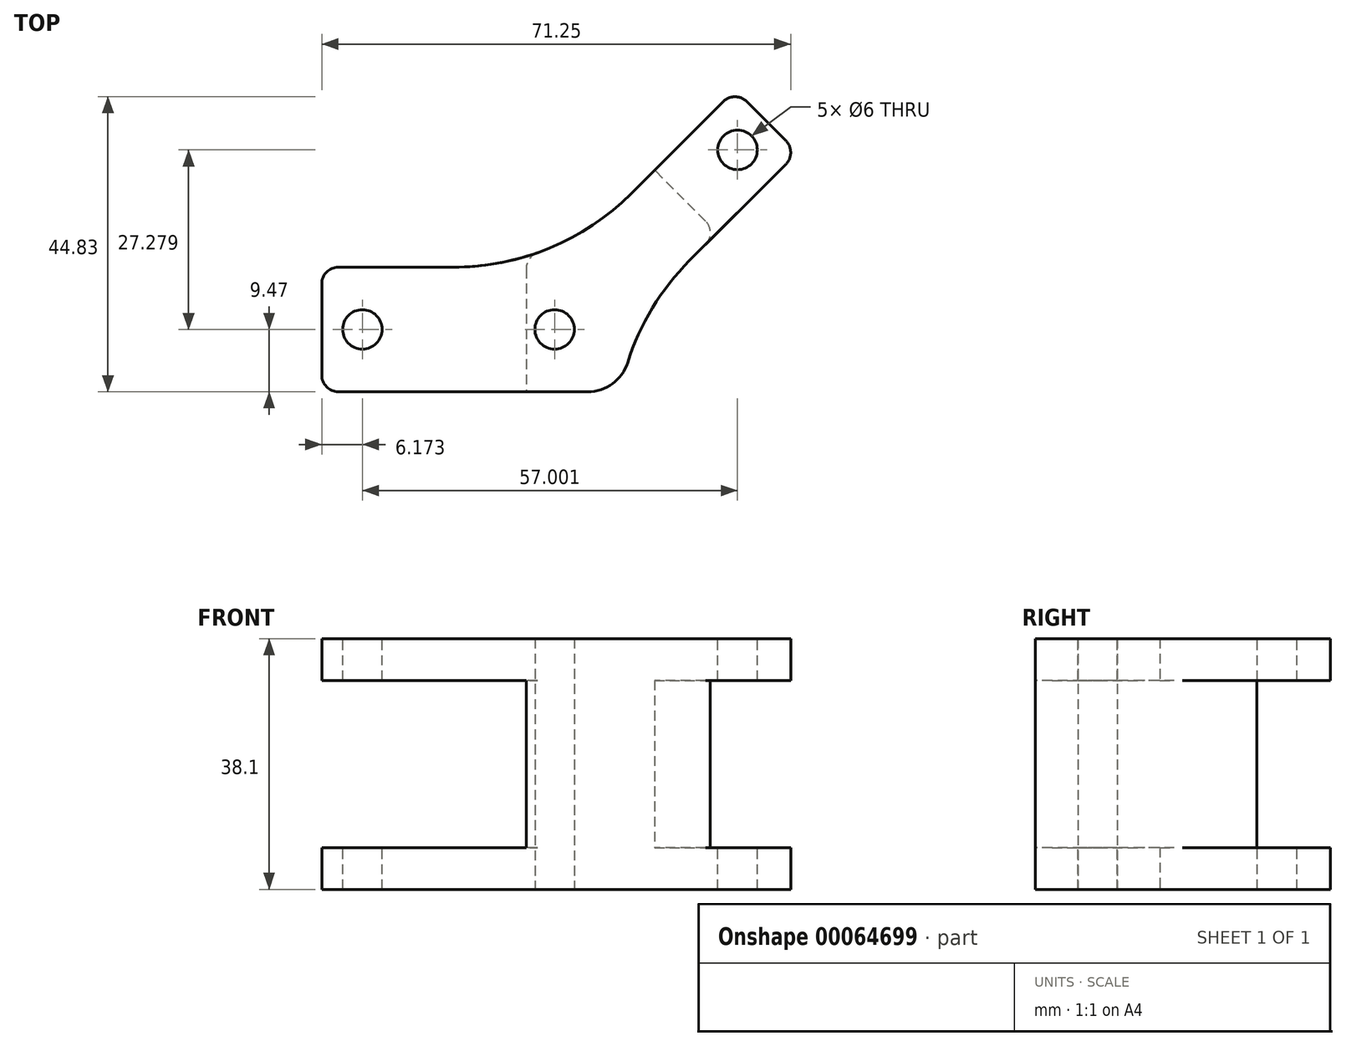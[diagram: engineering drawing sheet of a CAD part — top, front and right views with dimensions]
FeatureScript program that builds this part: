
annotation { "Feature Type Name" : "Feature", "Feature Type Description" : "" }
export const myFeature = defineFeature(function(context is Context, id is Id, definition is map)
    precondition{}
    {
        {
            var Q0;
            Q0=qCreatedBy(makeId("Top.planeOp"),FACE);
            var sketch = newSketch(context, id + "F0", { "sketchPlane" : qUnion([Q0])});
            skCircle(sketch, "E0", {"center": v(0, 0) * mm, "radius": 6 * mm});
            skLineSegment(sketch, "E1.rect.bottom", {"start": v(19.96, -18.93) * mm, "end": v(-19.96, -18.93) * mm});
            skLineSegment(sketch, "E1.rect.top", {"start": v(19.96, 18.93) * mm, "end": v(-19.96, 18.93) * mm});
            skLineSegment(sketch, "E1.rect.left", {"start": v(19.96, -18.93) * mm, "end": v(19.96, 18.93) * mm});
            skLineSegment(sketch, "E1.rect.right", {"start": v(-19.96, -18.93) * mm, "end": v(-19.96, 18.93) * mm});
            skSolve(sketch);
        }
        {
            var Q0;
            Q0=makeQuery(id+"F0.imprint","IMPRINT",FACE,{"disambiguationData":[TD([[makeQuery(id+"F0.imprint","IMPRINT",EDGE,{"derivedFrom":sQuery(id+"F0.wireOp",EDGE,"E0")}),-1.0]])]});
            extrude(context, id + "F1", {"entities" : qUnion([Q0]), "depth" : 76.2 * mm});
        }
        {
            var Q0;
            Q0=makeQuery(id+"F1.opExtrude","SWEPT_FACE",FACE,{"disambiguationData":[OSD([sQuery(id+"F0.wireOp",EDGE,"E1.rect.right")])]});
            extrude(context, id + "F2", {"entities" : qUnion([Q0]), "operationType" : NewBodyOperationType.ADD, "depth" : 38.1 * mm});
        }
        {
            var Q0;
            Q0=makeQuery(id+"F1.opExtrude","SWEPT_EDGE",EDGE,{"disambiguationData":[OSD([sQuery(id+"F0.wireOp",EDGE,"E1.rect.top"),sQuery(id+"F0.wireOp",EDGE,"E1.rect.left")])]});
            chamfer(context, id + "F3", {"entities" : qUnion([Q0]), "width" : 19.05 * mm, "tangentPropagation" : true});
        }
        {
            var Q0;
            Q0=makeQuery(id+"F3.opChamfer","BLEND_FACE",FACE,{"disambiguationData":[OSD([sQuery(id+"F0.wireOp",EDGE,"E1.rect.top"),sQuery(id+"F0.wireOp",EDGE,"E1.rect.left")])]});
            extrude(context, id + "F4", {"entities" : qUnion([Q0]), "operationType" : NewBodyOperationType.ADD, "depth" : 76.2 * mm});
        }
        {
            var Q0;
            {var subQ0=sQuery(id+"F0.wireOp",EDGE,"E1.rect.left");var subQ1=sQuery(id+"F0.wireOp",EDGE,"E1.rect.top");Q0=makeQuery(id+"F4.boolean.opBoolean","MERGE",EDGE,{"derivedFrom":[makeQuery(id+"F3.opChamfer","BLEND_EDGE",EDGE,{"blendedFrom":[makeQuery(id+"F1.opExtrude","SWEPT_EDGE",EDGE,{"disambiguationData":[OSD([subQ1,subQ0])]}),makeQuery(id+"F1.opExtrude","SWEPT_FACE",FACE,{"disambiguationData":[OSD([subQ0])]})],"blendedInto":[makeQuery(id+"F1.opExtrude","SWEPT_FACE",FACE,{"disambiguationData":[OSD([subQ0])]})]}),makeQuery(id+"F4.opExtrude","CAP_EDGE",EDGE,{"disambiguationData":[OSD([subQ1,subQ0])],"isStart":true})]});}
            fillet(context, id + "F5", {"entities" : qUnion([Q0]), "radius" : 76.2 * mm, "tangentPropagation" : true, "allowEdgeOverflow" : false});
        }
        {
            var Q0;
            {var subQ0=sQuery(id+"F0.wireOp",EDGE,"E1.rect.bottom");var subQ1=sQuery(id+"F0.wireOp",EDGE,"E1.rect.left");var subQ2=sQuery(id+"F0.wireOp",EDGE,"E1.rect.top");Q0=makeQuery(id+"F5.opFillet","BLEND_EDGE",EDGE,{"blendedFrom":[makeQuery(id+"F4.boolean.opBoolean","MERGE",EDGE,{"derivedFrom":[makeQuery(id+"F3.opChamfer","BLEND_EDGE",EDGE,{"blendedFrom":[makeQuery(id+"F1.opExtrude","SWEPT_EDGE",EDGE,{"disambiguationData":[OSD([subQ2,subQ1])]}),makeQuery(id+"F1.opExtrude","SWEPT_FACE",FACE,{"disambiguationData":[OSD([subQ1])]})],"blendedInto":[makeQuery(id+"F1.opExtrude","SWEPT_FACE",FACE,{"disambiguationData":[OSD([subQ1])]})]}),makeQuery(id+"F4.opExtrude","CAP_EDGE",EDGE,{"disambiguationData":[OSD([subQ2,subQ1])],"isStart":true})]}),makeQuery(id+"F2.boolean.opBoolean","MERGE",FACE,{"derivedFrom":[makeQuery(id+"F1.opExtrude","SWEPT_FACE",FACE,{"disambiguationData":[OSD([subQ0])]}),makeQuery(id+"F2.opExtrude","SWEPT_FACE",FACE,{"disambiguationData":[OSD([subQ0,sQuery(id+"F0.wireOp",EDGE,"E1.rect.right")])]})]})],"blendedInto":[makeQuery(id+"F2.boolean.opBoolean","MERGE",FACE,{"derivedFrom":[makeQuery(id+"F1.opExtrude","SWEPT_FACE",FACE,{"disambiguationData":[OSD([subQ0])]}),makeQuery(id+"F2.opExtrude","SWEPT_FACE",FACE,{"disambiguationData":[OSD([subQ0,sQuery(id+"F0.wireOp",EDGE,"E1.rect.right")])]})]})]});}
            fillet(context, id + "F6", {"entities" : qUnion([Q0]), "radius" : 12.7 * mm, "tangentPropagation" : true, "allowEdgeOverflow" : false});
        }
        {
            var Q0;
            {var subQ0=sQuery(id+"F0.wireOp",EDGE,"E1.rect.right");var subQ1=sQuery(id+"F0.wireOp",EDGE,"E1.rect.left");var subQ2=sQuery(id+"F0.wireOp",EDGE,"E1.rect.top");Q0=makeQuery(id+"F4.boolean.opBoolean","MERGE",EDGE,{"derivedFrom":[makeQuery(id+"F3.opChamfer","BLEND_EDGE",EDGE,{"blendedFrom":[makeQuery(id+"F1.opExtrude","SWEPT_EDGE",EDGE,{"disambiguationData":[OSD([subQ2,subQ1])]}),makeQuery(id+"F2.boolean.opBoolean","MERGE",FACE,{"derivedFrom":[makeQuery(id+"F1.opExtrude","SWEPT_FACE",FACE,{"disambiguationData":[OSD([subQ2])]}),makeQuery(id+"F2.opExtrude","SWEPT_FACE",FACE,{"disambiguationData":[OSD([subQ2,subQ0])]})]})],"blendedInto":[makeQuery(id+"F2.boolean.opBoolean","MERGE",FACE,{"derivedFrom":[makeQuery(id+"F1.opExtrude","SWEPT_FACE",FACE,{"disambiguationData":[OSD([subQ2])]}),makeQuery(id+"F2.opExtrude","SWEPT_FACE",FACE,{"disambiguationData":[OSD([subQ2,subQ0])]})]})]}),makeQuery(id+"F4.opExtrude","CAP_EDGE",EDGE,{"disambiguationData":[OSD([subQ2,subQ1,subQ0])],"isStart":true})]});}
            fillet(context, id + "F7", {"entities" : qUnion([Q0]), "radius" : 76.2 * mm, "tangentPropagation" : true, "allowEdgeOverflow" : false});
        }
        {
            var Q0;
            Q0=makeQuery(id+"F4.opExtrude","SWEPT_FACE",FACE,{"disambiguationData":[OSD([sQuery(id+"F0.wireOp",EDGE,"E1.rect.top"),sQuery(id+"F0.wireOp",EDGE,"E1.rect.left"),sQuery(id+"F0.wireOp",EDGE,"E1.rect.right")])]});
            var sketch = newSketch(context, id + "F8", { "sketchPlane" : qUnion([Q0])});
            skLineSegment(sketch, "E2.rect.bottom", {"start": v(-55.71, 63.5) * mm, "end": v(-124.76, 63.5) * mm});
            skLineSegment(sketch, "E2.rect.top", {"start": v(-55.71, 12.7) * mm, "end": v(-124.76, 12.7) * mm});
            skLineSegment(sketch, "E2.rect.left", {"start": v(-55.71, 63.5) * mm, "end": v(-55.71, 12.7) * mm});
            skLineSegment(sketch, "E2.rect.right", {"start": v(-124.76, 63.5) * mm, "end": v(-124.76, 12.7) * mm});
            skPoint(sketch, "E2.rect.middle", {"position": v(-90.23, 38.1) * mm});
            skSolve(sketch);
        }
        {
            var Q0;
            {var subQ0=sQuery(id+"F8.wireOp",EDGE,"E2.rect.left");Q0=makeQuery(id+"F8.imprint","IMPRINT",FACE,{"disambiguationData":[TD([[makeQuery(id+"F8.imprint","IMPRINT",EDGE,{"derivedFrom":subQ0}),-1.0]])]});}
            extrude(context, id + "F9", {"entities" : qUnion([Q0]), "operationType" : NewBodyOperationType.REMOVE, "oppositeDirection" : true, "depth" : 50.8 * mm});
        }
        {
            var Q0;
            {var subQ0=sQuery(id+"F0.wireOp",EDGE,"E1.rect.right");var subQ1=sQuery(id+"F0.wireOp",EDGE,"E1.rect.left");var subQ2=sQuery(id+"F0.wireOp",EDGE,"E1.rect.top");var subQ3=sQuery(id+"F0.wireOp",EDGE,"E1.rect.bottom");var subQ4=sQuery(id+"F0.wireOp",EDGE,"E0");var subQ5=makeQuery(id+"F2.boolean.opBoolean","MERGE",FACE,{"derivedFrom":[makeQuery(id+"F1.opExtrude","CAP_FACE",FACE,{"disambiguationData":[OSD([subQ4,subQ3,subQ2,subQ1,subQ0])],"isStart":false}),makeQuery(id+"F2.opExtrude","SWEPT_FACE",FACE,{"disambiguationData":[OSD([subQ0]),TDD([makeQuery(id+"F1.opExtrude","CAP_EDGE",EDGE,{"disambiguationData":[OSD([subQ0])],"isStart":false})])]})]});Q0=makeQuery(id+"F4.boolean.opBoolean","MERGE",FACE,{"derivedFrom":[subQ5,makeQuery(id+"F4.opExtrude","SWEPT_FACE",FACE,{"disambiguationData":[OSD([subQ4,subQ3,subQ2,subQ1,subQ0]),TDD([makeQuery(id+"F3.opChamfer","BLEND_EDGE",EDGE,{"blendedFrom":[makeQuery(id+"F1.opExtrude","SWEPT_EDGE",EDGE,{"disambiguationData":[OSD([subQ2,subQ1])]}),subQ5],"blendedInto":[subQ5]})])]})]});}
            var sketch = newSketch(context, id + "F10", { "sketchPlane" : qUnion([Q0])});
            skCircle(sketch, "E3", {"center": v(55.59, 54.56) * mm, "radius": 6 * mm});
            skSolve(sketch);
        }
        {
            var Q0;
            Q0 = qSketchRegion(id + "F10", true);
            extrude(context, id + "F11", {"entities" : qUnion([Q0]), "operationType" : NewBodyOperationType.REMOVE, "oppositeDirection" : true, "depth" : 106.15 * mm});
        }
        {
            var Q0;
            {var subQ2=sQuery(id+"F0.wireOp",EDGE,"E1.rect.left");var subQ3=sQuery(id+"F0.wireOp",EDGE,"E1.rect.top");Q0=makeQuery(id+"F9.boolean.opBoolean","SPLIT",EDGE,{"disambiguationData":[TD([makeQuery(id+"F9.opExtrude","SWEPT_FACE",FACE,{"disambiguationData":[OSD([sQuery(id+"F8.wireOp",EDGE,"E2.rect.bottom")])]})])],"derivedFrom":makeQuery(id+"F4.opExtrude","CAP_EDGE",EDGE,{"disambiguationData":[OSD([subQ3,subQ2])],"isStart":false})});}
            var Q1;
            {var subQ0=sQuery(id+"F0.wireOp",EDGE,"E1.rect.right");var subQ1=sQuery(id+"F0.wireOp",EDGE,"E1.rect.left");var subQ2=sQuery(id+"F0.wireOp",EDGE,"E1.rect.top");Q1=makeQuery(id+"F9.boolean.opBoolean","SPLIT",EDGE,{"disambiguationData":[TD([makeQuery(id+"F9.opExtrude","SWEPT_FACE",FACE,{"disambiguationData":[OSD([sQuery(id+"F8.wireOp",EDGE,"E2.rect.bottom")])]})])],"derivedFrom":makeQuery(id+"F4.opExtrude","CAP_EDGE",EDGE,{"disambiguationData":[OSD([subQ2,subQ1,subQ0])],"isStart":false})});}
            var Q2;
            {var subQ2=sQuery(id+"F0.wireOp",EDGE,"E1.rect.left");var subQ3=sQuery(id+"F0.wireOp",EDGE,"E1.rect.top");Q2=makeQuery(id+"F9.boolean.opBoolean","SPLIT",EDGE,{"disambiguationData":[TD([makeQuery(id+"F9.opExtrude","SWEPT_FACE",FACE,{"disambiguationData":[OSD([sQuery(id+"F8.wireOp",EDGE,"E2.rect.top")])]})])],"derivedFrom":makeQuery(id+"F4.opExtrude","CAP_EDGE",EDGE,{"disambiguationData":[OSD([subQ3,subQ2])],"isStart":false})});}
            var Q3;
            {var subQ0=sQuery(id+"F0.wireOp",EDGE,"E1.rect.right");var subQ1=sQuery(id+"F0.wireOp",EDGE,"E1.rect.left");var subQ2=sQuery(id+"F0.wireOp",EDGE,"E1.rect.top");Q3=makeQuery(id+"F9.boolean.opBoolean","SPLIT",EDGE,{"disambiguationData":[TD([makeQuery(id+"F9.opExtrude","SWEPT_FACE",FACE,{"disambiguationData":[OSD([sQuery(id+"F8.wireOp",EDGE,"E2.rect.top")])]})])],"derivedFrom":makeQuery(id+"F4.opExtrude","CAP_EDGE",EDGE,{"disambiguationData":[OSD([subQ2,subQ1,subQ0])],"isStart":false})});}
            fillet(context, id + "F12", {"entities" : qUnion([Q0, Q1, Q2, Q3]), "radius" : 5.08 * mm, "tangentPropagation" : true, "allowEdgeOverflow" : false});
        }
        {
            var Q0;
            {var subQ0=sQuery(id+"F0.wireOp",EDGE,"E1.rect.bottom");Q0=makeQuery(id+"F2.boolean.opBoolean","MERGE",FACE,{"derivedFrom":[makeQuery(id+"F1.opExtrude","SWEPT_FACE",FACE,{"disambiguationData":[OSD([subQ0])]}),makeQuery(id+"F2.opExtrude","SWEPT_FACE",FACE,{"disambiguationData":[OSD([subQ0,sQuery(id+"F0.wireOp",EDGE,"E1.rect.right")])]})]});}
            var sketch = newSketch(context, id + "F13", { "sketchPlane" : qUnion([Q0])});
            skLineSegment(sketch, "E4.rect.bottom", {"start": v(-8.6, 63.5) * mm, "end": v(-107.52, 63.5) * mm});
            skLineSegment(sketch, "E4.rect.top", {"start": v(-8.6, 12.7) * mm, "end": v(-107.52, 12.7) * mm});
            skLineSegment(sketch, "E4.rect.left", {"start": v(-8.6, 63.5) * mm, "end": v(-8.6, 12.7) * mm});
            skLineSegment(sketch, "E4.rect.right", {"start": v(-107.52, 63.5) * mm, "end": v(-107.52, 12.7) * mm});
            skPoint(sketch, "E4.rect.middle", {"position": v(-58.06, 38.1) * mm});
            skSolve(sketch);
        }
        {
            var Q0;
            Q0 = qSketchRegion(id + "F13", true);
            extrude(context, id + "F14", {"entities" : qUnion([Q0]), "operationType" : NewBodyOperationType.REMOVE, "oppositeDirection" : true, "depth" : 56.76 * mm});
        }
        {
            var Q0;
            {var subQ0=sQuery(id+"F0.wireOp",EDGE,"E1.rect.right");Q0=makeQuery(id+"F14.boolean.opBoolean","SPLIT",FACE,{"disambiguationData":[TD([makeQuery(id+"F14.opExtrude","SWEPT_FACE",FACE,{"disambiguationData":[OSD([sQuery(id+"F13.wireOp",EDGE,"E4.rect.bottom")])]})])],"derivedFrom":makeQuery(id+"F2.opExtrude","CAP_FACE",FACE,{"disambiguationData":[OSD([subQ0])],"isStart":false})});}
            var Q1;
            {var subQ0=sQuery(id+"F0.wireOp",EDGE,"E1.rect.right");Q1=makeQuery(id+"F14.boolean.opBoolean","SPLIT",FACE,{"disambiguationData":[TD([makeQuery(id+"F14.opExtrude","SWEPT_FACE",FACE,{"disambiguationData":[OSD([sQuery(id+"F13.wireOp",EDGE,"E4.rect.top")])]})])],"derivedFrom":makeQuery(id+"F2.opExtrude","CAP_FACE",FACE,{"disambiguationData":[OSD([subQ0])],"isStart":false})});}
            extrude(context, id + "F15", {"entities" : qUnion([Q0, Q1]), "operationType" : NewBodyOperationType.ADD, "depth" : 12.7 * mm});
        }
        {
            var Q0;
            {var subQ0=sQuery(id+"F0.wireOp",EDGE,"E1.rect.right");var subQ1=makeQuery(id+"F1.opExtrude","CAP_EDGE",EDGE,{"disambiguationData":[OSD([subQ0])],"isStart":false});var subQ2=sQuery(id+"F0.wireOp",EDGE,"E1.rect.left");var subQ3=sQuery(id+"F0.wireOp",EDGE,"E1.rect.top");var subQ4=sQuery(id+"F0.wireOp",EDGE,"E1.rect.bottom");var subQ5=sQuery(id+"F0.wireOp",EDGE,"E0");var subQ6=makeQuery(id+"F2.boolean.opBoolean","MERGE",FACE,{"derivedFrom":[makeQuery(id+"F1.opExtrude","CAP_FACE",FACE,{"disambiguationData":[OSD([subQ5,subQ4,subQ3,subQ2,subQ0])],"isStart":false}),makeQuery(id+"F2.opExtrude","SWEPT_FACE",FACE,{"disambiguationData":[OSD([subQ0]),TDD([subQ1])]})]});Q0=makeQuery(id+"F15.boolean.opBoolean","MERGE",FACE,{"derivedFrom":[makeQuery(id+"F4.boolean.opBoolean","MERGE",FACE,{"derivedFrom":[subQ6,makeQuery(id+"F4.opExtrude","SWEPT_FACE",FACE,{"disambiguationData":[OSD([subQ5,subQ4,subQ3,subQ2,subQ0]),TDD([makeQuery(id+"F3.opChamfer","BLEND_EDGE",EDGE,{"blendedFrom":[makeQuery(id+"F1.opExtrude","SWEPT_EDGE",EDGE,{"disambiguationData":[OSD([subQ3,subQ2])]}),subQ6],"blendedInto":[subQ6]})])]})]}),makeQuery(id+"F15.opExtrude","SWEPT_FACE",FACE,{"disambiguationData":[OSD([subQ0]),TDD([makeQuery(id+"F2.opExtrude","CAP_EDGE",EDGE,{"disambiguationData":[OSD([subQ0]),TDD([subQ1])],"isStart":false})])]})]});}
            var sketch = newSketch(context, id + "F16", { "sketchPlane" : qUnion([Q0])});
            skPoint(sketch, "E5.endSnap0", {"position": v(-70.76, 0) * mm});
            skCircle(sketch, "E6", {"center": v(-58.41, 0) * mm, "radius": 6 * mm});
            skSolve(sketch);
        }
        {
            var Q0;
            Q0 = qSketchRegion(id + "F16", true);
            extrude(context, id + "F17", {"entities" : qUnion([Q0]), "operationType" : NewBodyOperationType.REMOVE, "oppositeDirection" : true, "depth" : 143.58 * mm});
        }
        {
            var Q0;
            {var subQ0=sQuery(id+"F0.wireOp",EDGE,"E1.rect.right");var subQ2=sQuery(id+"F0.wireOp",EDGE,"E1.rect.bottom");Q0=makeQuery(id+"F15.opExtrude","CAP_EDGE",EDGE,{"disambiguationData":[OSD([subQ2,subQ0]),TDD([makeQuery(id+"F14.boolean.opBoolean","SPLIT",EDGE,{"disambiguationData":[TD([makeQuery(id+"F14.opExtrude","SWEPT_FACE",FACE,{"disambiguationData":[OSD([sQuery(id+"F13.wireOp",EDGE,"E4.rect.bottom")])]})])],"derivedFrom":makeQuery(id+"F2.opExtrude","CAP_EDGE",EDGE,{"disambiguationData":[OSD([subQ2,subQ0])],"isStart":false})})])],"isStart":false});}
            var Q1;
            {var subQ0=sQuery(id+"F0.wireOp",EDGE,"E1.rect.right");var subQ2=sQuery(id+"F0.wireOp",EDGE,"E1.rect.bottom");Q1=makeQuery(id+"F15.opExtrude","CAP_EDGE",EDGE,{"disambiguationData":[OSD([subQ2,subQ0]),TDD([makeQuery(id+"F14.boolean.opBoolean","SPLIT",EDGE,{"disambiguationData":[TD([makeQuery(id+"F14.opExtrude","SWEPT_FACE",FACE,{"disambiguationData":[OSD([sQuery(id+"F13.wireOp",EDGE,"E4.rect.top")])]})])],"derivedFrom":makeQuery(id+"F2.opExtrude","CAP_EDGE",EDGE,{"disambiguationData":[OSD([subQ2,subQ0])],"isStart":false})})])],"isStart":false});}
            var Q2;
            {var subQ0=sQuery(id+"F0.wireOp",EDGE,"E1.rect.right");var subQ2=sQuery(id+"F0.wireOp",EDGE,"E1.rect.top");Q2=makeQuery(id+"F15.opExtrude","CAP_EDGE",EDGE,{"disambiguationData":[OSD([subQ2,subQ0]),TDD([makeQuery(id+"F14.boolean.opBoolean","SPLIT",EDGE,{"disambiguationData":[TD([makeQuery(id+"F14.opExtrude","SWEPT_FACE",FACE,{"disambiguationData":[OSD([sQuery(id+"F13.wireOp",EDGE,"E4.rect.top")])]})])],"derivedFrom":makeQuery(id+"F2.opExtrude","CAP_EDGE",EDGE,{"disambiguationData":[OSD([subQ2,subQ0])],"isStart":false})})])],"isStart":false});}
            var Q3;
            {var subQ0=sQuery(id+"F0.wireOp",EDGE,"E1.rect.right");var subQ2=sQuery(id+"F0.wireOp",EDGE,"E1.rect.top");Q3=makeQuery(id+"F15.opExtrude","CAP_EDGE",EDGE,{"disambiguationData":[OSD([subQ2,subQ0]),TDD([makeQuery(id+"F14.boolean.opBoolean","SPLIT",EDGE,{"disambiguationData":[TD([makeQuery(id+"F14.opExtrude","SWEPT_FACE",FACE,{"disambiguationData":[OSD([sQuery(id+"F13.wireOp",EDGE,"E4.rect.bottom")])]})])],"derivedFrom":makeQuery(id+"F2.opExtrude","CAP_EDGE",EDGE,{"disambiguationData":[OSD([subQ2,subQ0])],"isStart":false})})])],"isStart":false});}
            var Q4;
            Q4=makeQuery(id+"F14.boolean.opBoolean","INTERSECT",EDGE,{"derivedFrom":[makeQuery(id+"F7.opFillet","BLEND_FACE",FACE,{"disambiguationData":[OSD([sQuery(id+"F0.wireOp",EDGE,"E1.rect.top"),sQuery(id+"F0.wireOp",EDGE,"E1.rect.left"),sQuery(id+"F0.wireOp",EDGE,"E1.rect.right")])]}),makeQuery(id+"F14.opExtrude","SWEPT_FACE",FACE,{"disambiguationData":[OSD([sQuery(id+"F13.wireOp",EDGE,"E4.rect.left")])]})]});
            var Q5;
            Q5=makeQuery(id+"F14.boolean.opBoolean","COPY",EDGE,{"derivedFrom":makeQuery(id+"F14.opExtrude","CAP_EDGE",EDGE,{"disambiguationData":[OSD([sQuery(id+"F13.wireOp",EDGE,"E4.rect.left")])],"isStart":true})});
            var Q6;
            Q6=makeQuery(id+"F9.boolean.opBoolean","COPY",EDGE,{"derivedFrom":makeQuery(id+"F9.opExtrude","CAP_EDGE",EDGE,{"disambiguationData":[OSD([sQuery(id+"F8.wireOp",EDGE,"E2.rect.left")])],"isStart":true})});
            var Q7;
            Q7=makeQuery(id+"F9.boolean.opBoolean","INTERSECT",EDGE,{"derivedFrom":[makeQuery(id+"F4.opExtrude","SWEPT_FACE",FACE,{"disambiguationData":[OSD([sQuery(id+"F0.wireOp",EDGE,"E1.rect.top"),sQuery(id+"F0.wireOp",EDGE,"E1.rect.left")])]}),makeQuery(id+"F9.opExtrude","SWEPT_FACE",FACE,{"disambiguationData":[OSD([sQuery(id+"F8.wireOp",EDGE,"E2.rect.left")])]})]});
            fillet(context, id + "F18", {"entities" : qUnion([Q0, Q1, Q2, Q3, Q4, Q5, Q6, Q7]), "radius" : 5.08 * mm, "tangentPropagation" : true, "allowEdgeOverflow" : false});
        }
        {
            var Q0;
            Q0=makeQuery(id+"F1.opExtrude","SWEPT_BODY",BODY,{"disambiguationData":[OSD([sQuery(id+"F0.wireOp",EDGE,"E0"),sQuery(id+"F0.wireOp",EDGE,"E1.rect.bottom"),sQuery(id+"F0.wireOp",EDGE,"E1.rect.top"),sQuery(id+"F0.wireOp",EDGE,"E1.rect.left"),sQuery(id+"F0.wireOp",EDGE,"E1.rect.right")])]});
            var Q1;
            Q1=qCreatedBy(makeId("Origin.pointOp"),VERTEX);
            transform(context, id + "F19", {"entities" : qUnion([Q0]), "transformType" : TransformType.SCALE_UNIFORMLY, "scale" : 1, "scalePoint" : qUnion([Q1]), "makeCopy" : false});
        }
        {
            var Q0;
            Q0=makeQuery(id+"F1.opExtrude","SWEPT_BODY",BODY,{"disambiguationData":[OSD([sQuery(id+"F0.wireOp",EDGE,"E0"),sQuery(id+"F0.wireOp",EDGE,"E1.rect.bottom"),sQuery(id+"F0.wireOp",EDGE,"E1.rect.top"),sQuery(id+"F0.wireOp",EDGE,"E1.rect.left"),sQuery(id+"F0.wireOp",EDGE,"E1.rect.right")])]});
            var Q1;
            Q1=qCreatedBy(makeId("Origin.pointOp"),VERTEX);
            transform(context, id + "F20", {"entities" : qUnion([Q0]), "transformType" : TransformType.SCALE_UNIFORMLY, "scale" : .5, "scalePoint" : qUnion([Q1]), "makeCopy" : false});
        }
    });
